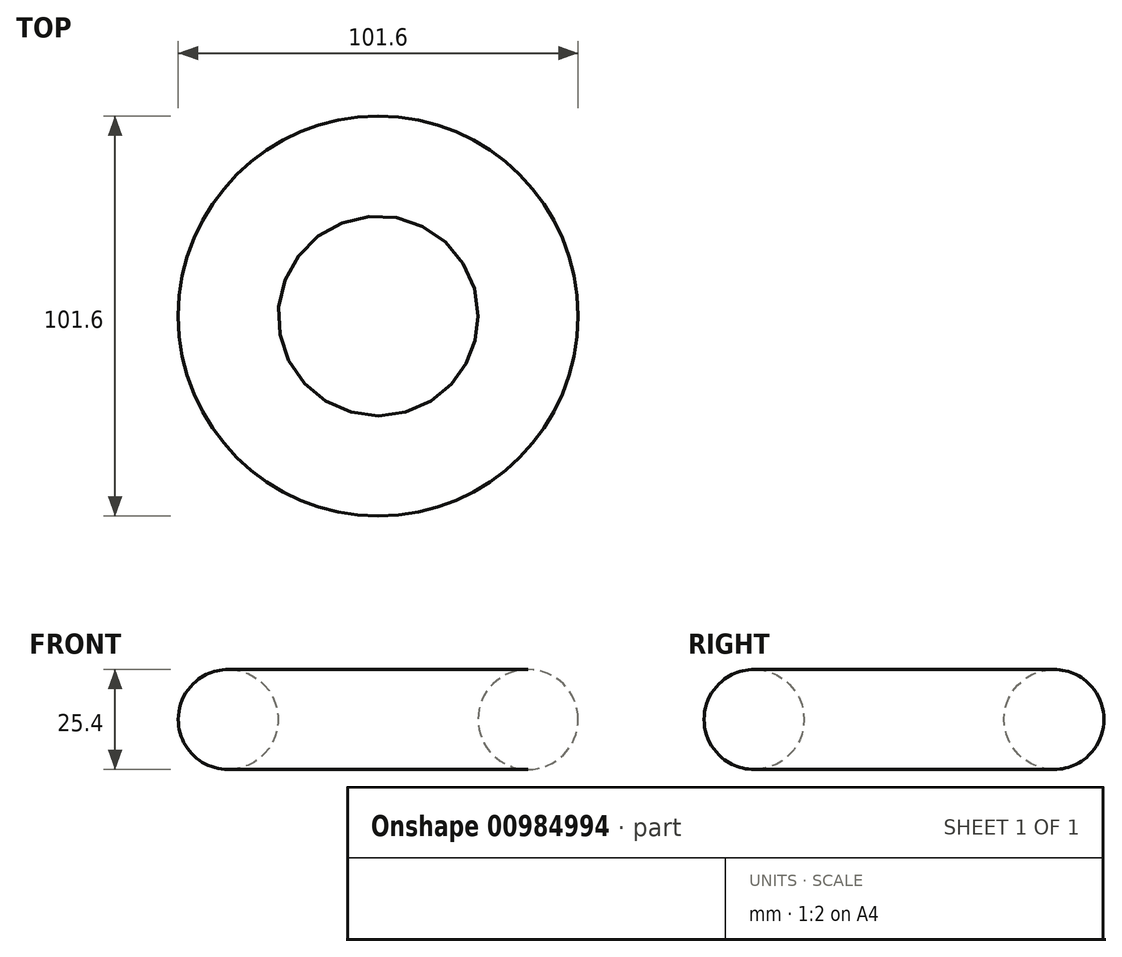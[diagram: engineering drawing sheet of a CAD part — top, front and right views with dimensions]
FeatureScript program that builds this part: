
annotation { "Feature Type Name" : "Feature", "Feature Type Description" : "" }
export const myFeature = defineFeature(function(context is Context, id is Id, definition is map)
    precondition{}
    {
        {
            var Q0;
            Q0=qCreatedBy(makeId("Front.planeOp"),FACE);
            var sketch = newSketch(context, id + "F0", { "sketchPlane" : qUnion([Q0])});
            skLineSegment(sketch, "E0", {"start": v(0, 12.7) * mm, "end": v(0, -12.7) * mm, "construction": true});
            skCircle(sketch, "E1", {"center": v(38.1, 0) * mm, "radius": 12.7 * mm});
            skSolve(sketch);
        }
        {
            var Q0;
            Q0=makeQuery(id+"F0.imprint","IMPRINT",FACE,{"disambiguationData":[TD([[makeQuery(id+"F0.imprint","IMPRINT",EDGE,{"derivedFrom":sQuery(id+"F0.wireOp",EDGE,"E1")}),1.0]])]});
            var Q1;
            Q1=sQuery(id+"F0.wireOp",EDGE,"E0");
            revolve(context, id + "F1", {"surfaceOperationType" : NewSurfaceOperationType.NEW, "entities" : qUnion([Q0]), "axis" : qUnion([Q1]), "revolveType" : RevolveType.FULL});
        }
    });
